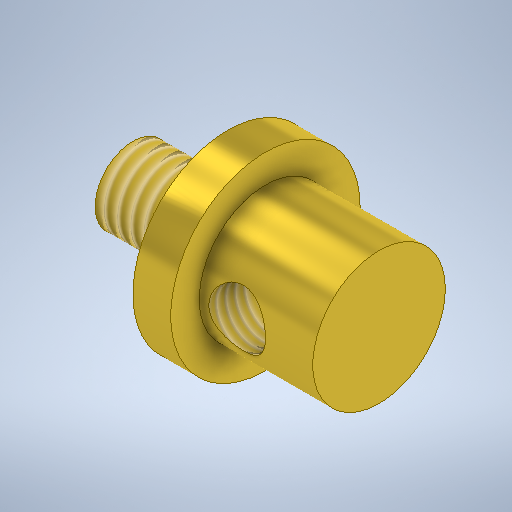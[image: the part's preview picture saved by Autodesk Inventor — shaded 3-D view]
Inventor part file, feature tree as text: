
AUTODESK INVENTOR PART (.ipt)
format: ipt  version: 2025.1 (Build 291241000, 241)  size: 311,808 bytes
history: native  units: mm
features: thread x2, sketch x2, revolve x1, plane x1, hole x1
ambient origin geometry x8: Origin, YZ Plane, XZ Plane, XY Plane, X Axis, Y Axis, Z Axis, Center Point
bodies: Solid1 (feature_tree)
feature tree (7):
  revolve  "Revolution1"  [1 undecoded]
  thread  "Thread1"  [1 undecoded]
  plane  "Work Plane3"
  hole  "Hole1"  [1 undecoded]
  thread  "Thread2"  [1 undecoded]
  sketch  "Sketch1"  dims[d0=4.0mm d1=5.0mm d2=2.0mm]
  sketch  "Sketch5"  dims[d3=10.0mm d4=7.0mm d5=6.0mm d6=90.0deg d7=10.0mm d8=0.0mm d12=-3.5mm d13=4.0mm d14=3.0mm d15=6.0mm d16=4.0mm d17=2.0mm d18=90.0deg d19=2.5mm d20=0.0mm d21=10.0mm d22=0.0mm]
note: 4 required parameter values undecoded (feature->parameter linkage not recoverable at this tier; creation-order binding heuristic only, values carry confidence <= 0.55)